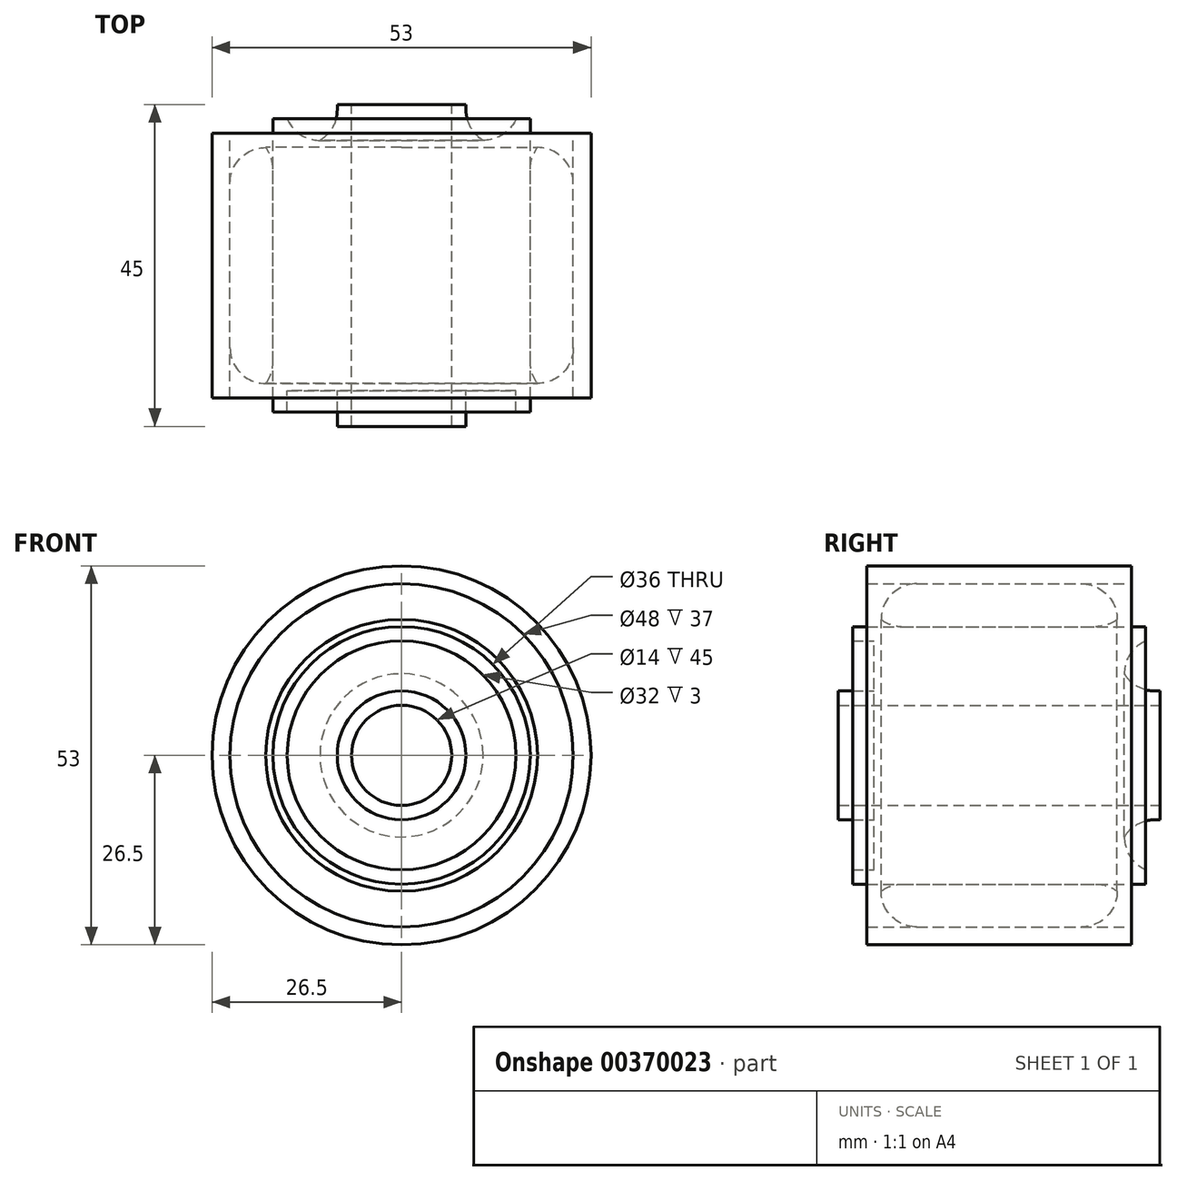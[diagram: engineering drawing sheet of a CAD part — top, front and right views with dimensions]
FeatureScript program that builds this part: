
annotation { "Feature Type Name" : "Feature", "Feature Type Description" : "" }
export const myFeature = defineFeature(function(context is Context, id is Id, definition is map)
    precondition{}
    {
        {
            var Q0;
            Q0=qCreatedBy(makeId("Front.planeOp"),FACE);
            var sketch = newSketch(context, id + "F0", { "sketchPlane" : qUnion([Q0])});
            skCircle(sketch, "E0", {"center": v(0, 0) * mm, "radius": 7 * mm});
            skCircle(sketch, "E1", {"center": v(0, 0) * mm, "radius": 9 * mm});
            skSolve(sketch);
        }
        {
            var Q0;
            Q0=qSketchRegion(id+"F0",true);
            extrude(context, id + "F1", {"entities" : qUnion([Q0]), "depth" : 45 * mm});
        }
        {
            var Q0;
            Q0=qCreatedBy(makeId("Front.planeOp"),FACE);
            cPlane(context, id + "F2", {"entities" : qUnion([Q0]), "cplaneType" : CPlaneType.OFFSET, "offset" : 5 * mm, "width" : 150 * mm, "height" : 150 * mm});
        }
        {
            var Q0;
            Q0=qCreatedBy(id+"F2.planeOp",FACE);
            var sketch = newSketch(context, id + "F3", { "sketchPlane" : qUnion([Q0])});
            skCircle(sketch, "E2", {"center": v(0, 0) * mm, "radius": 9 * mm});
            skCircle(sketch, "E3", {"center": v(0, 0) * mm, "radius": 16 * mm});
            skSolve(sketch);
        }
        {
            var Q0;
            Q0=qSketchRegion(id+"F3",true);
            var Q1;
            Q1=makeQuery(id+"F3.imprint","IMPRINT",FACE,{"disambiguationData":[TD([[makeQuery(id+"F3.imprint","IMPRINT",EDGE,{"derivedFrom":sQuery(id+"F3.wireOp",EDGE,"E2")}),-1.0]])]});
            extrude(context, id + "F4", {"entities" : qUnion([Q0, Q1]), "operationType" : NewBodyOperationType.ADD, "depth" : 35 * mm});
        }
        {
            var Q0;
            Q0=qCreatedBy(makeId("Front.planeOp"),FACE);
            cPlane(context, id + "F5", {"entities" : qUnion([Q0]), "cplaneType" : CPlaneType.OFFSET, "offset" : 2 * mm, "width" : 150 * mm, "height" : 150 * mm});
        }
        {
            var Q0;
            Q0=qCreatedBy(id+"F5.planeOp",FACE);
            var sketch = newSketch(context, id + "F6", { "sketchPlane" : qUnion([Q0])});
            skCircle(sketch, "E4", {"center": v(0, 0) * mm, "radius": 16 * mm});
            skCircle(sketch, "E5", {"center": v(0, 0) * mm, "radius": 18 * mm});
            skSolve(sketch);
        }
        {
            var Q0;
            Q0=qSketchRegion(id+"F6",true);
            extrude(context, id + "F7", {"entities" : qUnion([Q0]), "operationType" : NewBodyOperationType.ADD, "depth" : 41 * mm});
        }
        {
            var Q0;
            Q0=qCreatedBy(makeId("Front.planeOp"),FACE);
            cPlane(context, id + "F8", {"entities" : qUnion([Q0]), "cplaneType" : CPlaneType.OFFSET, "offset" : 4 * mm, "width" : 150 * mm, "height" : 150 * mm});
        }
        {
            var Q0;
            Q0=qCreatedBy(id+"F8.planeOp",FACE);
            var sketch = newSketch(context, id + "F9", { "sketchPlane" : qUnion([Q0])});
            skCircle(sketch, "E6", {"center": v(0, 0) * mm, "radius": 24 * mm});
            skCircle(sketch, "E7", {"center": v(0, 0) * mm, "radius": 26.5 * mm});
            skSolve(sketch);
        }
        {
            var Q0;
            Q0=qSketchRegion(id+"F9",true);
            extrude(context, id + "F10", {"entities" : qUnion([Q0]), "depth" : 37 * mm});
        }
        {
            var Q0;
            Q0=qCreatedBy(makeId("Front.planeOp"),FACE);
            cPlane(context, id + "F11", {"entities" : qUnion([Q0]), "cplaneType" : CPlaneType.OFFSET, "offset" : 6 * mm, "width" : 150 * mm, "height" : 150 * mm});
        }
        {
            var Q0;
            Q0=qCreatedBy(id+"F11.planeOp",FACE);
            var sketch = newSketch(context, id + "F12", { "sketchPlane" : qUnion([Q0])});
            skCircle(sketch, "E8", {"center": v(0, 0) * mm, "radius": 18 * mm});
            skCircle(sketch, "E9", {"center": v(0, 0) * mm, "radius": 24 * mm});
            skSolve(sketch);
        }
        {
            var Q0;
            Q0=qSketchRegion(id+"F12",true);
            extrude(context, id + "F13", {"entities" : qUnion([Q0]), "depth" : 33 * mm});
        }
        {
            var Q0;
            Q0=makeQuery(id+"F4.opExtrude","CAP_EDGE",EDGE,{"disambiguationData":[OSD([sQuery(id+"F3.wireOp",EDGE,"E3")])],"isStart":false});
            var Q1;
            Q1=makeQuery(id+"F13.opExtrude","CAP_EDGE",EDGE,{"disambiguationData":[OSD([sQuery(id+"F12.wireOp",EDGE,"E9")])],"isStart":false});
            fillet(context, id + "F14", {"entities" : qUnion([Q0, Q1]), "radius" : 5 * mm, "tangentPropagation" : true, "allowEdgeOverflow" : false});
        }
        {
            var Q0;
            Q0=makeQuery(id+"F4.opExtrude","CAP_EDGE",EDGE,{"disambiguationData":[OSD([sQuery(id+"F3.wireOp",EDGE,"E2")])],"isStart":false});
            var Q1;
            Q1=makeQuery(id+"F13.opExtrude","CAP_EDGE",EDGE,{"disambiguationData":[OSD([sQuery(id+"F12.wireOp",EDGE,"E8")])],"isStart":false});
            fillet(context, id + "F15", {"entities" : qUnion([Q0, Q1]), "radius" : 5 * mm, "tangentPropagation" : true, "allowEdgeOverflow" : false});
        }
        {
            var Q0;
            Q0=makeQuery(id+"F4.opExtrude","CAP_EDGE",EDGE,{"disambiguationData":[OSD([sQuery(id+"F3.wireOp",EDGE,"E3")])],"isStart":true});
            var Q1;
            Q1=makeQuery(id+"F13.opExtrude","CAP_EDGE",EDGE,{"disambiguationData":[OSD([sQuery(id+"F12.wireOp",EDGE,"E9")])],"isStart":true});
            fillet(context, id + "F16", {"entities" : qUnion([Q0, Q1]), "radius" : 5 * mm, "tangentPropagation" : true, "allowEdgeOverflow" : false});
        }
        {
            var Q0;
            Q0=makeQuery(id+"F4.opExtrude","CAP_EDGE",EDGE,{"disambiguationData":[OSD([sQuery(id+"F3.wireOp",EDGE,"E2")])],"isStart":true});
            var Q1;
            Q1=makeQuery(id+"F13.opExtrude","CAP_EDGE",EDGE,{"disambiguationData":[OSD([sQuery(id+"F12.wireOp",EDGE,"E8")])],"isStart":true});
            fillet(context, id + "F17", {"entities" : qUnion([Q0, Q1]), "radius" : 5 * mm, "tangentPropagation" : true, "allowEdgeOverflow" : false});
        }
    });
